# Revit family: Door_Sectional_Clopay_Insulated-HorizontalTrack
name_source: partatom
category: Doors
units: mm (PartAtom-declared; Revit-internal decimal feet)

## family parameters
Always vertical = Yes
Cut with Voids When Loaded = No
Host = Wall
OmniClass Number = 23.30.10.17.37.14
OmniClass Title = Sectional Overhead Doors
Room Calculation Point = No
Shared = No

## types (1)
- ByType
    3211 Spacing = Yes
    ADA Compliant = Yes
    Assembly Code = B2030410
    Breakaway Bottom Section = No
    Construction Details = http://www.arcat.com
    Description = Clopay Overhead Door as Specified
    Door Glazing = Glass - Insulated - Clopay - Clear Tempered
    Door Height = 12' - 0"
    Door Width = 12' - 2"
    Expected Lifespan (Years) = 0
    Frame Finish = Metal - Steel - Clopay - Stucco Emboss - Tan
    Frame Thickness = 0' - 4 3/4"
    Function = Interior
    Green Building-LEED = http://www.arcat.com
    Hardware Finish = Metal - Steel - Clopay - Galvanized
    Height = 12' - 0"
    Keynote = 08360
    Maintenance Schedule (Months) = 0
    Manufacturer = Clopay Building Products Company
    Manufacturer Fax = 513-770-3519
    Manufacturer Website = http://www.arcat.com
    Maximum Size = Consult Clopay Specifications & Shop Drawings
    Model = As Specified
    NumPanels = 7
    NumPanels_3211 = 7
    NumPanels_Standard = 6
    Opening Height = 12' - 0"
    Opening Width = 12' - 0"
    P10 = No
    P11 = No
    P4 = Yes
    P5 = Yes
    P6 = Yes
    P7 = Yes
    P8 = No
    P9 = No
    Panel Height = 1' - 8 9/16"
    Panel Material = Metal - Steel - Clopay - Stucco Emboss - Tan
    Pass Door = Yes
    Product Data = http://www.arcat.com
    RO Offset = 0' - 0"
    R_Value = 0
    Revision = R1_09-2011
    Rough Height = 12' - 0"
    Rough Width = 12' - 0"
    Sales Information = http://www.clopaydoor.com
    Send Message = http://www.clopaydoor.com
    Sound Transmission Class (STC) = 0
    SpecWizard = http://www.arcat.com
    Specification = http://www.arcat.com
    Thickness = 0' - 1 3/4"
    Track Offset = 0' - 1"
    URL = http://www.clopaydoor.com
    Wall Closure = By host
    Warranty Duration (Years) = 0
    Width = 12' - 0"

## geometry (parser evidence)
native form markers: Blend x54, Sweep x23
no freeform markers — native parametric forms only
